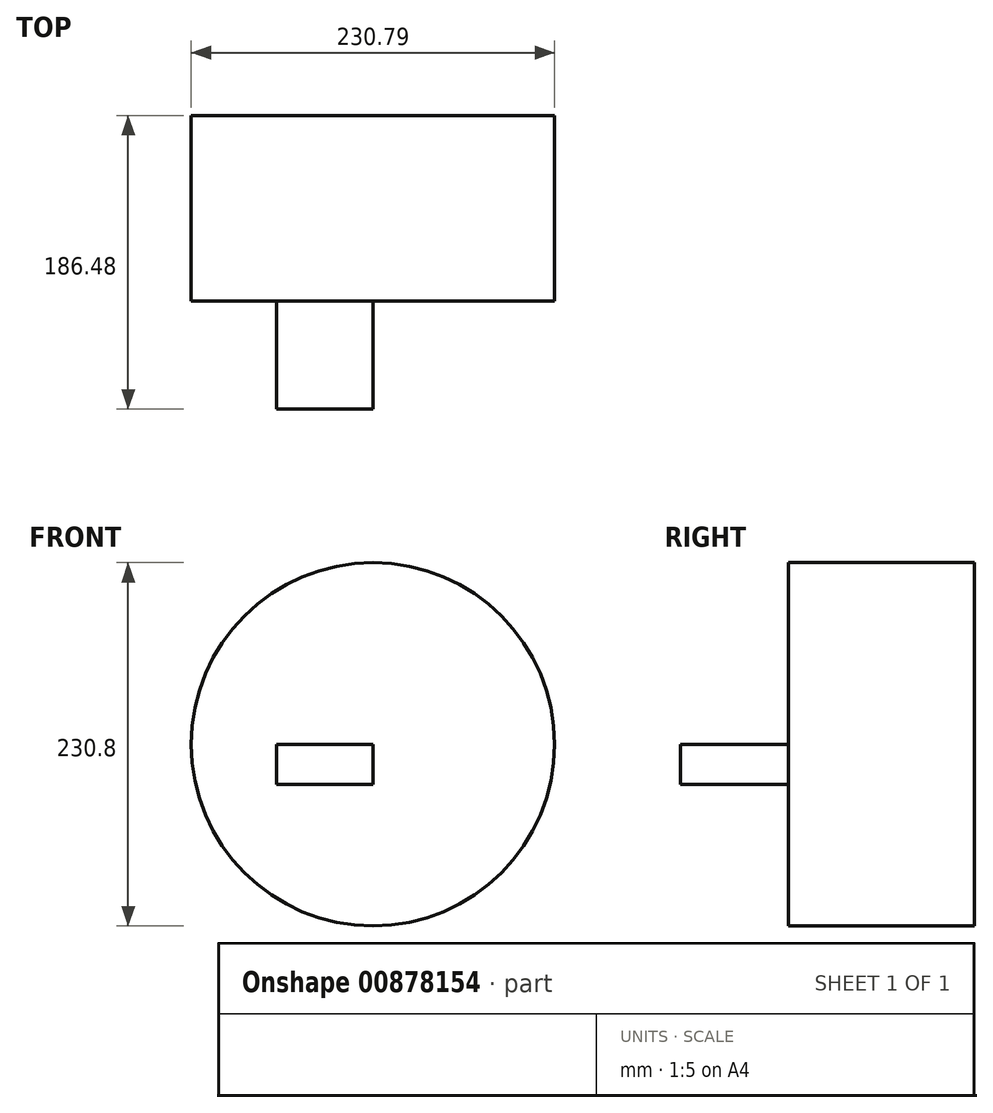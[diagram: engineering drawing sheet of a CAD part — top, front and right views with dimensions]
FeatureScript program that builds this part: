
annotation { "Feature Type Name" : "Feature", "Feature Type Description" : "" }
export const myFeature = defineFeature(function(context is Context, id is Id, definition is map)
    precondition{}
    {
        {
            var Q0;
            Q0=qCreatedBy(makeId("Top.planeOp"),FACE);
            var sketch = newSketch(context, id + "F0", { "sketchPlane" : qUnion([Q0])});
            skLineSegment(sketch, "E0.bottom", {"start": v(0, 68.53) * mm, "end": v(61.14, 68.53) * mm});
            skLineSegment(sketch, "E0.top", {"start": v(0, 0) * mm, "end": v(61.14, 0) * mm});
            skLineSegment(sketch, "E0.left", {"start": v(0, 68.53) * mm, "end": v(0, 0) * mm});
            skLineSegment(sketch, "E0.right", {"start": v(61.14, 68.53) * mm, "end": v(61.14, 0) * mm});
            skSolve(sketch);
        }
        {
            var Q0;
            Q0 = qSketchRegion(id + "F0", true);
            extrude(context, id + "F1", {"entities" : qUnion([Q0]), "depth" : 25.4 * mm, "offsetDistance" : 25.4 * mm});
        }
        {
            var Q0;
            Q0=makeQuery(id+"F1.opExtrude","CAP_FACE",FACE,{"disambiguationData":[OSD([sQuery(id+"F0.wireOp",EDGE,"E0.bottom"),sQuery(id+"F0.wireOp",EDGE,"E0.top"),sQuery(id+"F0.wireOp",EDGE,"E0.left"),sQuery(id+"F0.wireOp",EDGE,"E0.right")])],"isStart":false});
            var sketch = newSketch(context, id + "F2", { "sketchPlane" : qUnion([Q0])});
            skLineSegment(sketch, "E1.bottom", {"start": v(61.14, 68.53) * mm, "end": v(176.53, 68.53) * mm});
            skLineSegment(sketch, "E1.top", {"start": v(61.14, 186.48) * mm, "end": v(176.53, 186.48) * mm});
            skLineSegment(sketch, "E1.left", {"start": v(61.14, 68.53) * mm, "end": v(61.14, 186.48) * mm});
            skLineSegment(sketch, "E1.right", {"start": v(176.53, 68.53) * mm, "end": v(176.53, 186.48) * mm});
            skSolve(sketch);
        }
        {
            var Q0;
            Q0=makeQuery(id+"F2.imprint","IMPRINT",FACE,{"disambiguationData":[TD([[makeQuery(id+"F2.imprint","IMPRINT",EDGE,{"derivedFrom":makeQuery(id+"F1.opExtrude","CAP_EDGE",EDGE,{"disambiguationData":[OSD([sQuery(id+"F0.wireOp",EDGE,"E0.bottom")])],"isStart":false})}),-1.0]])]});
            var sketch = newSketch(context, id + "F3", { "sketchPlane" : qUnion([Q0])});
            skCircle(sketch, "E2", {"center": v(59.64, 71.5) * mm, "radius": 127 * mm});
            skSolve(sketch);
        }
        {
            var Q0;
            Q0=makeQuery(id+"F2.imprint","IMPRINT",FACE,{"disambiguationData":[TD([[makeQuery(id+"F2.imprint","IMPRINT",EDGE,{"derivedFrom":sQuery(id+"F2.wireOp",EDGE,"E1.bottom")}),1.0]])]});
            var Q1;
            Q1=makeQuery(id+"F1.opExtrude","CAP_EDGE",EDGE,{"disambiguationData":[OSD([sQuery(id+"F0.wireOp",EDGE,"E0.right")])],"isStart":false});
            revolve(context, id + "F4", {"operationType" : NewBodyOperationType.ADD, "surfaceOperationType" : NewSurfaceOperationType.NEW, "entities" : qUnion([Q0]), "axis" : qUnion([Q1]), "revolveType" : RevolveType.FULL});
        }
        {
            var Q0;
            Q0=sQuery(id+"F3.wireOp",EDGE,"E2");
            extrude(context, id + "F5", {"bodyType" : ToolBodyType.SURFACE, "surfaceEntities" : qUnion([Q0]), "depth" : 50.8 * mm, "offsetDistance" : 25.4 * mm});
        }
    });
